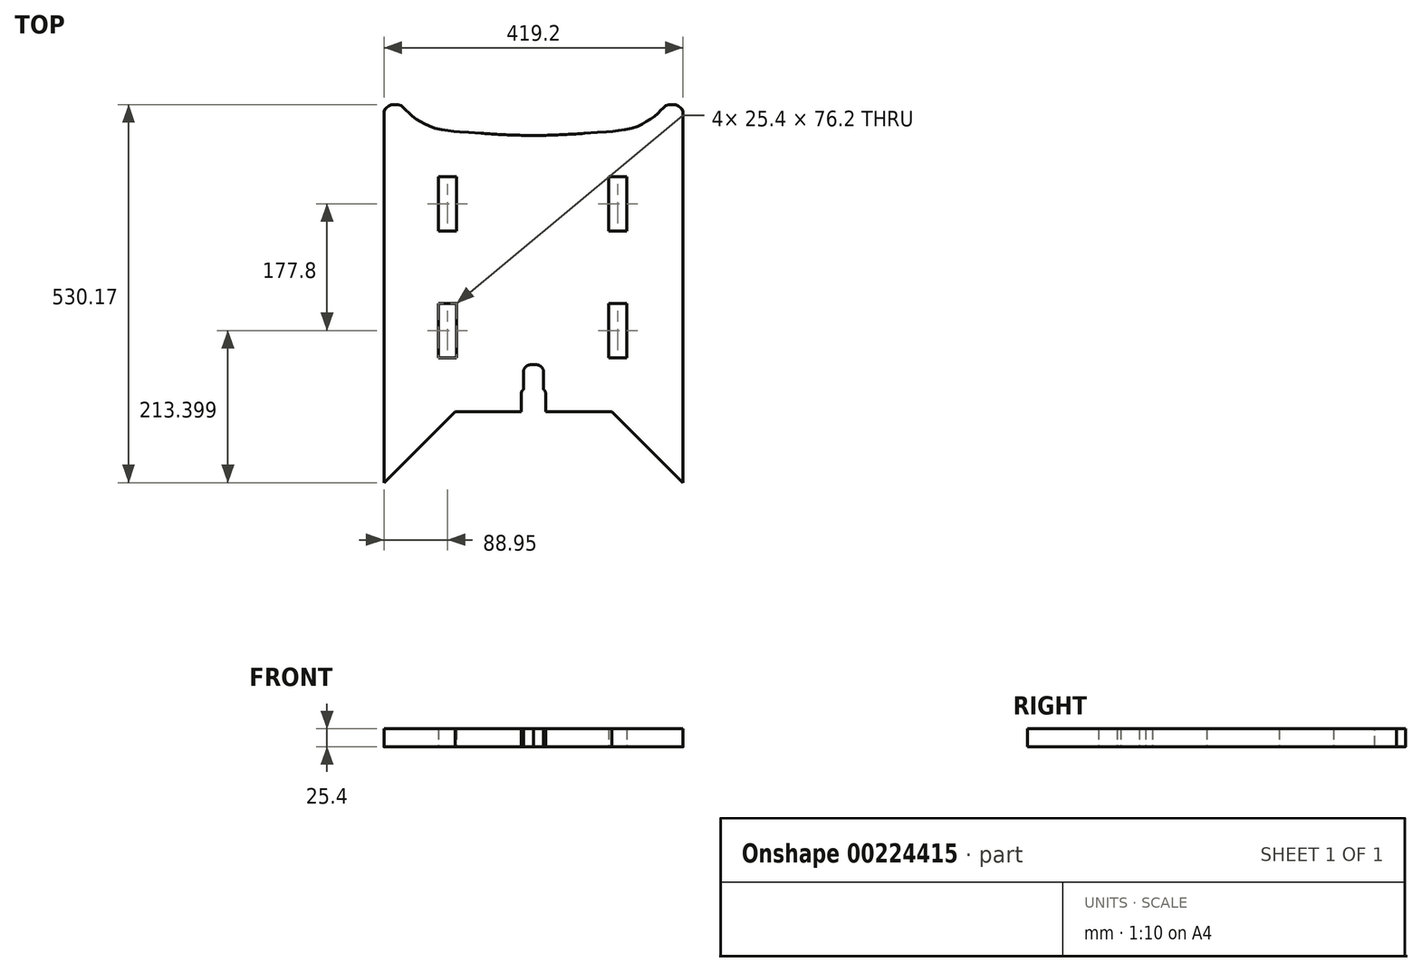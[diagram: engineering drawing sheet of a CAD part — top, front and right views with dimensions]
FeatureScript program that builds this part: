
annotation { "Feature Type Name" : "Feature", "Feature Type Description" : "" }
export const myFeature = defineFeature(function(context is Context, id is Id, definition is map)
    precondition{}
    {
        {
            var Q0;
            Q0=qCreatedBy(makeId("Top.planeOp"),FACE);
            var sketch = newSketch(context, id + "F0", { "sketchPlane" : qUnion([Q0])});
            skLineSegment(sketch, "E0", {"start": v(419.1, 29.16) * mm, "end": v(419.1, 0) * mm});
            skLineSegment(sketch, "E1", {"start": v(419.1, 0) * mm, "end": v(319.4, 99.46) * mm});
            skLineSegment(sketch, "E2", {"start": v(319.4, 99.46) * mm, "end": v(238.1, 99.46) * mm});
            skLineSegment(sketch, "E3.MirrorCS", {"start": v(99.7, 99.46) * mm, "end": v(181, 99.46) * mm});
            skLineSegment(sketch, "E4.MirrorCS", {"start": v(0, 0) * mm, "end": v(99.7, 99.46) * mm});
            skLineSegment(sketch, "E5.MirrorCS", {"start": v(0, 29.16) * mm, "end": v(0, 0) * mm});
            skLineSegment(sketch, "E6", {"start": v(0, 29.16) * mm, "end": v(0, 517.3) * mm});
            skLineSegment(sketch, "E7", {"start": v(0, 517.3) * mm, "end": v(0, 29.16) * mm});
            skFitSpline(sketch, "E8", {"points": [v(0, 517.3) * mm, v(0, 519.83) * mm, v(0.64, 522.4) * mm, v(1.74, 524.26) * mm, v(3.21, 525.8) * mm, v(5.79, 528.12) * mm, v(9.64, 529.73) * mm, v(14.2, 530.11) * mm, v(20.76, 529.92) * mm, v(25.13, 528.06) * mm, v(28.47, 524.71) * mm, v(32.78, 520.6) * mm, v(39.98, 513.6) * mm, v(49.04, 507.75) * mm, v(58.23, 502.22) * mm, v(73.08, 496.84) * mm, v(93.35, 493.2) * mm, v(111.79, 491.62) * mm, v(208.44, 486.94) * mm], "startDerivative": vector(-4.81, 90.89) * mm, "endDerivative": vector(535.6, 1.58) * mm});
            skLineSegment(sketch, "E9", {"start": v(192.48, 99.46) * mm, "end": v(192.48, 125.58) * mm});
            skFitSpline(sketch, "E10", {"points": [v(192.48, 125.58) * mm, v(193.49, 128.67) * mm, v(195.54, 130.72) * mm], "startDerivative": vector(1.38, 6.46) * mm, "endDerivative": vector(4.78, 3.8) * mm});
            skLineSegment(sketch, "E11", {"start": v(195.54, 130.72) * mm, "end": v(195.54, 157.12) * mm});
            skFitSpline(sketch, "E12", {"points": [v(195.54, 157.12) * mm, v(197.09, 160.56) * mm, v(200.3, 163.65) * mm, v(204.3, 165.25) * mm, v(209.55, 165.48) * mm], "startDerivative": vector(5.32, 15.26) * mm, "endDerivative": vector(20, -0.36) * mm});
            skFitSpline(sketch, "E13.MirrorCS", {"points": [v(226.62, 125.58) * mm, v(225.61, 128.67) * mm, v(223.56, 130.72) * mm], "startDerivative": vector(-1.38, 6.46) * mm, "endDerivative": vector(-4.78, 3.8) * mm});
            skFitSpline(sketch, "E14.MirrorCS", {"points": [v(223.56, 157.12) * mm, v(222.01, 160.56) * mm, v(218.8, 163.65) * mm, v(214.8, 165.25) * mm, v(209.55, 165.48) * mm], "startDerivative": vector(-5.32, 15.26) * mm, "endDerivative": vector(-20, -0.36) * mm});
            skLineSegment(sketch, "E15.MirrorCS", {"start": v(419.1, 29.16) * mm, "end": v(419.1, 517.3) * mm});
            skLineSegment(sketch, "E16.MirrorCS", {"start": v(223.56, 130.72) * mm, "end": v(223.56, 157.12) * mm});
            skFitSpline(sketch, "E17.MirrorCS", {"points": [v(419.1, 517.3) * mm, v(419.1, 519.83) * mm, v(418.46, 522.4) * mm, v(417.36, 524.26) * mm, v(415.89, 525.8) * mm, v(413.31, 528.12) * mm, v(409.46, 529.73) * mm, v(404.9, 530.11) * mm, v(398.34, 529.92) * mm, v(393.97, 528.06) * mm, v(390.63, 524.71) * mm, v(386.32, 520.6) * mm, v(379.12, 513.6) * mm, v(370.06, 507.75) * mm, v(360.87, 502.22) * mm, v(346.02, 496.84) * mm, v(325.75, 493.2) * mm, v(307.31, 491.62) * mm, v(208.44, 486.94) * mm], "startDerivative": vector(4.81, 90.89) * mm, "endDerivative": vector(-535.6, 1.58) * mm});
            skLineSegment(sketch, "E18.MirrorCS", {"start": v(226.62, 99.46) * mm, "end": v(226.62, 125.58) * mm});
            skLineSegment(sketch, "E19.MirrorCS", {"start": v(419.1, 517.3) * mm, "end": v(419.1, 29.16) * mm});
            skLineSegment(sketch, "E20", {"start": v(181, 99.46) * mm, "end": v(192.48, 99.46) * mm});
            skLineSegment(sketch, "E21.trimOffspring", {"start": v(226.62, 99.46) * mm, "end": v(238.1, 99.46) * mm});
            skLineSegment(sketch, "E22", {"start": v(208.44, 467.89) * mm, "end": v(259.24, 467.89) * mm});
            skLineSegment(sketch, "E23", {"start": v(259.24, 467.89) * mm, "end": v(157.64, 467.89) * mm});
            skLineSegment(sketch, "E24", {"start": v(136.09, 489.91) * mm, "end": v(157.64, 467.89) * mm});
            skLineSegment(sketch, "E25.MirrorCS", {"start": v(280.6, 489.8) * mm, "end": v(259.24, 467.89) * mm});
            skLineSegment(sketch, "E26.bottom", {"start": v(101.6, 353.1) * mm, "end": v(76.2, 353.1) * mm});
            skLineSegment(sketch, "E26.top", {"start": v(101.6, 429.3) * mm, "end": v(76.2, 429.3) * mm});
            skLineSegment(sketch, "E26.left", {"start": v(101.6, 353.1) * mm, "end": v(101.6, 429.3) * mm});
            skLineSegment(sketch, "E26.right", {"start": v(76.2, 353.1) * mm, "end": v(76.2, 429.3) * mm});
            skPoint(sketch, "E26.middle", {"position": v(88.9, 391.2) * mm});
            skLineSegment(sketch, "E27.bottom", {"start": v(101.6, 251.5) * mm, "end": v(76.2, 251.5) * mm});
            skLineSegment(sketch, "E27.top", {"start": v(101.6, 175.3) * mm, "end": v(76.2, 175.3) * mm});
            skLineSegment(sketch, "E27.left", {"start": v(101.6, 251.5) * mm, "end": v(101.6, 175.3) * mm});
            skLineSegment(sketch, "E27.right", {"start": v(76.2, 251.5) * mm, "end": v(76.2, 175.3) * mm});
            skPoint(sketch, "E27.middle", {"position": v(88.9, 213.4) * mm});
            skPoint(sketch, "E28.MirrorP", {"position": v(327.97, 213.4) * mm});
            skLineSegment(sketch, "E29.MirrorCS", {"start": v(315.27, 175.3) * mm, "end": v(340.67, 175.3) * mm});
            skLineSegment(sketch, "E30.MirrorCS", {"start": v(315.27, 353.1) * mm, "end": v(340.67, 353.1) * mm});
            skLineSegment(sketch, "E31.MirrorCS", {"start": v(315.27, 429.3) * mm, "end": v(340.67, 429.3) * mm});
            skLineSegment(sketch, "E32.MirrorCS", {"start": v(340.67, 353.1) * mm, "end": v(340.67, 429.3) * mm});
            skLineSegment(sketch, "E33.MirrorCS", {"start": v(315.27, 251.5) * mm, "end": v(315.27, 175.3) * mm});
            skLineSegment(sketch, "E34.MirrorCS", {"start": v(315.27, 353.1) * mm, "end": v(315.27, 429.3) * mm});
            skLineSegment(sketch, "E35.MirrorCS", {"start": v(315.27, 251.5) * mm, "end": v(340.67, 251.5) * mm});
            skLineSegment(sketch, "E36.MirrorCS", {"start": v(340.67, 251.5) * mm, "end": v(340.67, 175.3) * mm});
            skPoint(sketch, "E37.MirrorP", {"position": v(327.97, 391.2) * mm});
            skSolve(sketch);
        }
        {
            var Q0;
            Q0 = qSketchRegion(id + "F0", true);
            extrude(context, id + "F1", {"entities" : qUnion([Q0]), "depth" : 25.4 * mm});
        }
    });
